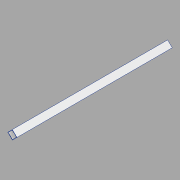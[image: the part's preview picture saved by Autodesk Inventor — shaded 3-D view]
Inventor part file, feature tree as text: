
AUTODESK INVENTOR PART (.ipt)
format: ipt  version: 2020 (Build 240168000, 168)  size: 81,920 bytes
history: native  units: in
note: dims shown in document units (in); Inventor stores cm internally (conversion verified against a paired STEP export)
features: extrude x1, shell x1, sketch x1
ambient origin geometry x8: Origin, YZ Plane, XZ Plane, XY Plane, X Axis, Y Axis, Z Axis, Center Point
bodies: Solid1 (feature_tree)
feature tree (3):
  extrude  "Extrusion1"  Depth=1.0in
  shell  "Shell1"  Thickness=24.0in
  sketch  "Sketch1"  dims[d2=1.0in d3=1.0in d4=24.0in d5=0.0in d6=0.05in]
